# Revit family: Zumtobel MIREL-L DI L1348
name_source: partatom
category: Lighting Fixtures
revit_build: Autodesk Revit 2014 (Build: 20140709_2115(x64)
units: mm (PartAtom-declared; Revit-internal decimal feet)

## types (1)
- MIREL- L DI LED840 EVG ASQ1
    Apparent Load = 58 VA
    Assembly Code = D5020200
    Color Filter = 16777215
    Default Elevation = 0 mm  [stored 0 ft]
    Description = Surface mount LED luminaire
    Dimming Lamp Color Temperature Shift = <None>
    Emit Shape Visible in Rendering = No
    Emit from Rectangle Length = 238 mm  [stored 0.78084 ft]
    Emit from Rectangle Width = 1348 mm  [stored 4.42257 ft]
    Height = 52 mm
    Lamp = LED
    Length = 1348 mm  [stored 4.42257 ft]
    Manufacturer = Zumtobel Lighting
    Model = 42183049
    Photometric Web File = 42183049_(STD).IES
    Tilt Angle = 90.00°
    URL = http://www.zumtobel.com
    Voltage = 230 V
    Width = 238 mm  [stored 0.78084 ft]

note: [stored X ft] marks values corroborated as IEEE doubles in the binary element streams (Revit-internal decimal feet)

## geometry (parser evidence)
native form markers: Sweep x2
no freeform markers — native parametric forms only
